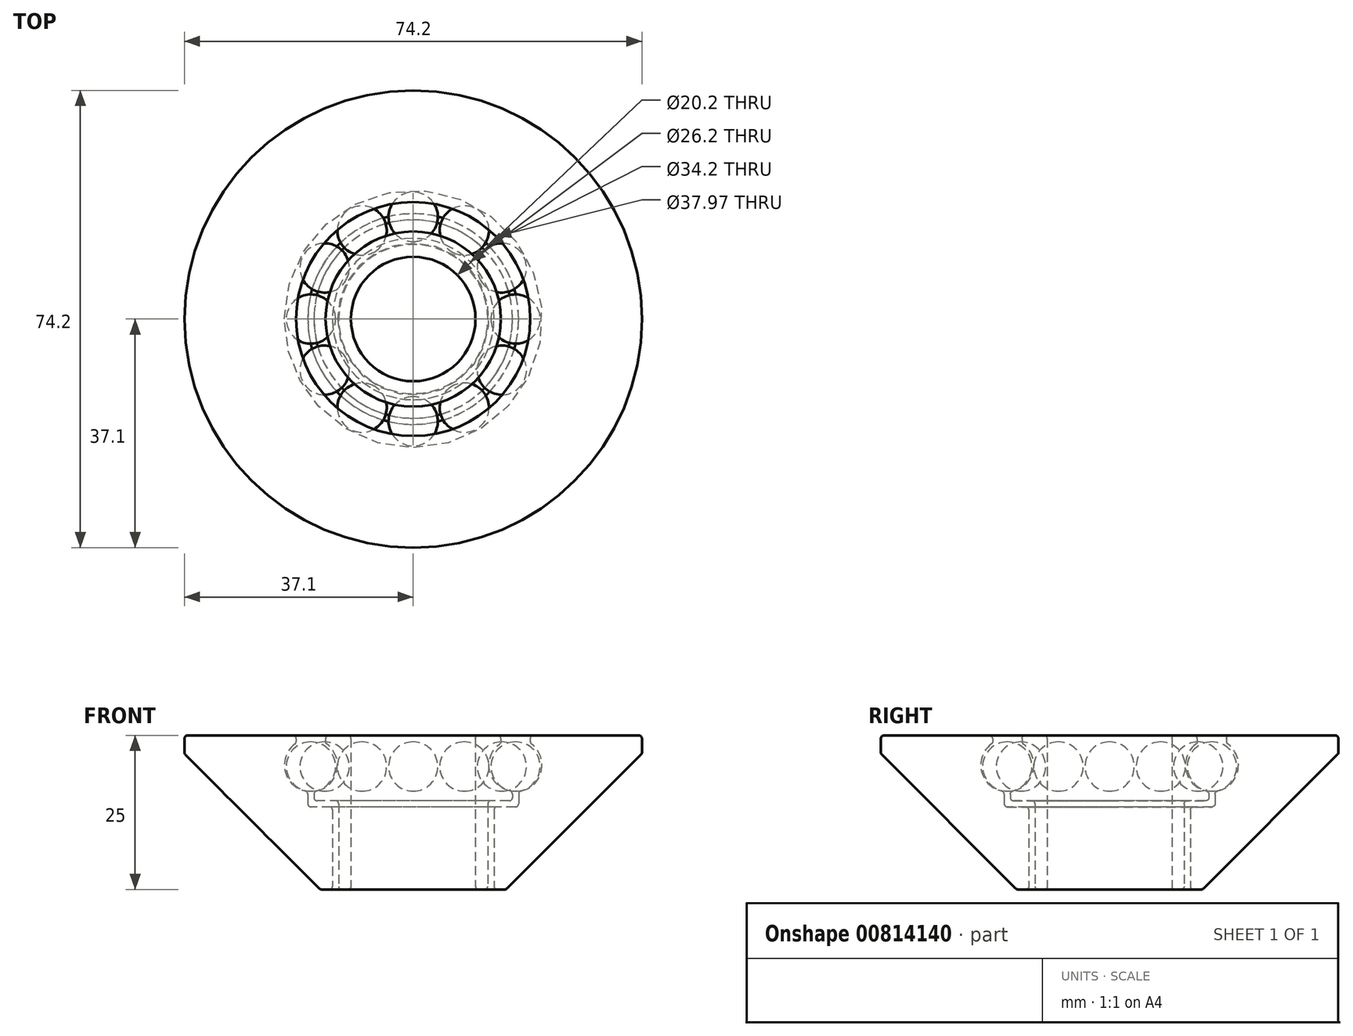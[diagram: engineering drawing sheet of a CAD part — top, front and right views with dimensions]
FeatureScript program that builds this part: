
annotation { "Feature Type Name" : "Feature", "Feature Type Description" : "" }
export const myFeature = defineFeature(function(context is Context, id is Id, definition is map)
    precondition{}
    {
        {
            var Q0;
            Q0=qCreatedBy(makeId("Front.planeOp"),FACE);
            var sketch = newSketch(context, id + "F0", { "sketchPlane" : qUnion([Q0])});
            skLineSegment(sketch, "E0", {"start": v(0, -18.14) * mm, "end": v(0, 38.96) * mm, "construction": true});
            skLineSegment(sketch, "E1", {"start": v(-10.1, 0) * mm, "end": v(-10.1, 25) * mm});
            skLineSegment(sketch, "E2", {"start": v(-10.1, 25) * mm, "end": v(-14.22, 25) * mm});
            skLineSegment(sketch, "E3", {"start": v(-16.1, 25) * mm, "end": v(-16.1, 24.14) * mm});
            skLineSegment(sketch, "E4", {"start": v(-16.1, 14.4) * mm, "end": v(-12.1, 14.4) * mm});
            skLineSegment(sketch, "E5", {"start": v(-12.1, 14.4) * mm, "end": v(-12.1, 0) * mm});
            skLineSegment(sketch, "E6", {"start": v(-12.1, 0) * mm, "end": v(-10.1, 0) * mm});
            skLineSegment(sketch, "E7", {"start": v(-13.1, 13.4) * mm, "end": v(-13.1, 0) * mm});
            skLineSegment(sketch, "E8", {"start": v(-13.1, 0) * mm, "end": v(-15.1, 0) * mm});
            skLineSegment(sketch, "E9", {"start": v(-15.1, 0) * mm, "end": v(-37.1, 22) * mm});
            skLineSegment(sketch, "E10", {"start": v(-37.1, 22) * mm, "end": v(-37.1, 25) * mm});
            skLineSegment(sketch, "E11", {"start": v(-37.1, 25) * mm, "end": v(-18.98, 25) * mm});
            skLineSegment(sketch, "E12", {"start": v(-17.1, 25) * mm, "end": v(-17.1, 24.14) * mm});
            skLineSegment(sketch, "E13", {"start": v(-17.1, 13.4) * mm, "end": v(-13.1, 13.4) * mm});
            skCircle(sketch, "E14", {"center": v(-16.6, 20.17) * mm, "radius": 4 * mm, "construction": true});
            skArc(sketch, "E15", {"start": v(-16.1, 15.9) * mm, "mid": v(-12.42, 19.17) * mm, "end": v(-14.22, 23.75) * mm});
            skLineSegment(sketch, "E16.trimOffspring", {"start": v(-16.1, 15.9) * mm, "end": v(-16.1, 14.4) * mm});
            skLineSegment(sketch, "E17.trimOffspring", {"start": v(-17.1, 15.9) * mm, "end": v(-17.1, 13.4) * mm});
            skArc(sketch, "E18.trimOffspring", {"start": v(-18.98, 23.75) * mm, "mid": v(-20.78, 19.17) * mm, "end": v(-17.1, 15.9) * mm});
            skLineSegment(sketch, "E19", {"start": v(-14.22, 25) * mm, "end": v(-14.22, 23.75) * mm});
            skLineSegment(sketch, "E20", {"start": v(-18.98, 25) * mm, "end": v(-18.98, 23.75) * mm});
            skSolve(sketch);
        }
        {
            var Q0;
            Q0=makeQuery(id+"F0.imprint","IMPRINT",FACE,{"disambiguationData":[TD([[makeQuery(id+"F0.imprint","IMPRINT",EDGE,{"derivedFrom":sQuery(id+"F0.wireOp",EDGE,"E7")}),-1.0]])]});
            var Q1;
            Q1=makeQuery(id+"F0.imprint","IMPRINT",FACE,{"disambiguationData":[TD([[makeQuery(id+"F0.imprint","IMPRINT",EDGE,{"derivedFrom":sQuery(id+"F0.wireOp",EDGE,"E1")}),1.0]])]});
            var Q2;
            Q2=sQuery(id+"F0.wireOp",EDGE,"E0");
            revolve(context, id + "F1", {"surfaceOperationType" : NewSurfaceOperationType.NEW, "entities" : qUnion([Q0, Q1]), "axis" : qUnion([Q2]), "revolveType" : RevolveType.FULL});
        }
        {
            var Q0;
            Q0=qCreatedBy(makeId("Front.planeOp"),FACE);
            var sketch = newSketch(context, id + "F2", { "sketchPlane" : qUnion([Q0])});
            skLineSegment(sketch, "E21", {"start": v(-16.6, 23.95) * mm, "end": v(-16.6, 15.95) * mm});
            skArc(sketch, "E22", {"start": v(-16.6, 15.95) * mm, "mid": v(-20.6, 19.95) * mm, "end": v(-16.6, 23.95) * mm});
            skLineSegment(sketch, "E23", {"start": v(0, -3.32) * mm, "end": v(0, 31.05) * mm, "construction": true});
            skSolve(sketch);
        }
        {
            var Q0;
            Q0 = qSketchRegion(id + "F2", true);
            var Q1;
            Q1=sQuery(id+"F2.wireOp",EDGE,"E21");
            revolve(context, id + "F3", {"surfaceOperationType" : NewSurfaceOperationType.NEW, "entities" : qUnion([Q0]), "axis" : qUnion([Q1]), "revolveType" : RevolveType.FULL});
        }
        {
            var Q0;
            Q0=makeQuery(id+"F3.opRevolve","SWEPT_BODY",BODY,{"disambiguationData":[OSD([sQuery(id+"F2.wireOp",EDGE,"E21"),sQuery(id+"F2.wireOp",EDGE,"E22")])]});
            var Q1;
            Q1=sQuery(id+"F0.wireOp",EDGE,"E0");
            circularPattern(context, id + "F4", {"entities" : qUnion([Q0]), "axis" : qUnion([Q1]), "angle" : 360 * degree, "instanceCount" : 12, "equalSpace" : true});
        }
        {
            var Q0;
            Q0=makeQuery(id+"F1.opRevolve","SWEPT_FACE",FACE,{"disambiguationData":[OSD([sQuery(id+"F0.wireOp",EDGE,"E11")])]});
            var Q1;
            Q1=makeQuery(id+"F1.opRevolve","SWEPT_FACE",FACE,{"disambiguationData":[OSD([sQuery(id+"F0.wireOp",EDGE,"E9")])]});
            var Q2;
            Q2=makeQuery(id+"F1.opRevolve","SWEPT_FACE",FACE,{"disambiguationData":[OSD([sQuery(id+"F0.wireOp",EDGE,"E6")])]});
            var Q3;
            Q3=makeQuery(id+"F1.opRevolve","SWEPT_EDGE",EDGE,{"disambiguationData":[OSD([sQuery(id+"F0.wireOp",EDGE,"E7"),sQuery(id+"F0.wireOp",EDGE,"E8")])]});
            var Q4;
            Q4=makeQuery(id+"F1.opRevolve","SWEPT_FACE",FACE,{"disambiguationData":[OSD([sQuery(id+"F0.wireOp",EDGE,"E2")])]});
            var Q5;
            Q5=makeQuery(id+"F1.opRevolve","SWEPT_EDGE",EDGE,{"disambiguationData":[OSD([sQuery(id+"F0.wireOp",EDGE,"E15"),sQuery(id+"F0.wireOp",EDGE,"E19")])]});
            var Q6;
            Q6=makeQuery(id+"F1.opRevolve","SWEPT_EDGE",EDGE,{"disambiguationData":[OSD([sQuery(id+"F0.wireOp",EDGE,"E18.trimOffspring"),sQuery(id+"F0.wireOp",EDGE,"E20")])]});
            var Q7;
            Q7=makeQuery(id+"F1.opRevolve","SWEPT_FACE",FACE,{"disambiguationData":[OSD([sQuery(id+"F0.wireOp",EDGE,"E16.trimOffspring")])]});
            var Q8;
            Q8=makeQuery(id+"F1.opRevolve","SWEPT_EDGE",EDGE,{"disambiguationData":[OSD([sQuery(id+"F0.wireOp",EDGE,"E4"),sQuery(id+"F0.wireOp",EDGE,"E5")])]});
            var Q9;
            Q9=makeQuery(id+"F1.opRevolve","SWEPT_EDGE",EDGE,{"disambiguationData":[OSD([sQuery(id+"F0.wireOp",EDGE,"E7"),sQuery(id+"F0.wireOp",EDGE,"E13")])]});
            var Q10;
            Q10=makeQuery(id+"F1.opRevolve","SWEPT_FACE",FACE,{"disambiguationData":[OSD([sQuery(id+"F0.wireOp",EDGE,"E17.trimOffspring")])]});
            fillet(context, id + "F5", {"entities" : qUnion([Q0, Q1, Q2, Q3, Q4, Q5, Q6, Q7, Q8, Q9, Q10]), "radius" : .5 * mm, "tangentPropagation" : true, "allowEdgeOverflow" : false});
        }
    });
